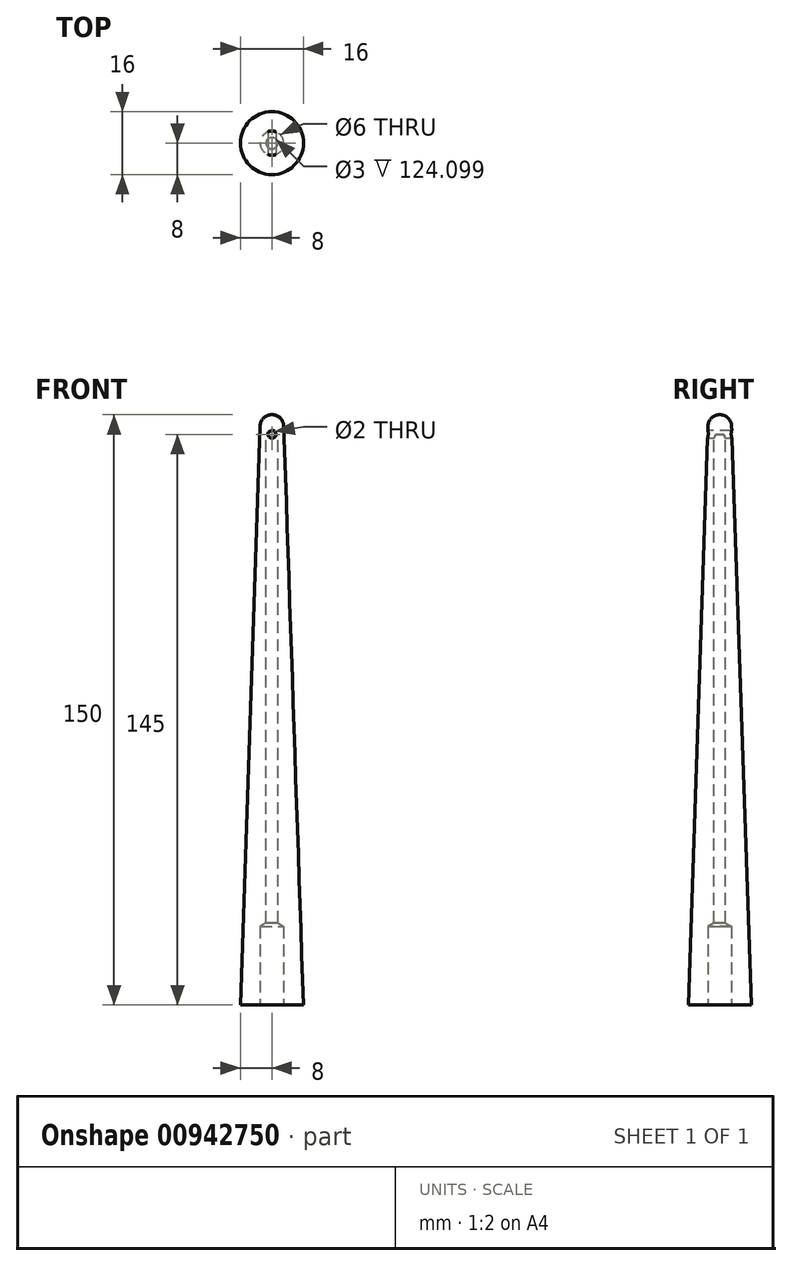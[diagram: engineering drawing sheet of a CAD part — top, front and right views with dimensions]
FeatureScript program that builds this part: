
annotation { "Feature Type Name" : "Feature", "Feature Type Description" : "" }
export const myFeature = defineFeature(function(context is Context, id is Id, definition is map)
    precondition{}
    {
        {
            var Q0;
            Q0=qCreatedBy(makeId("Front.planeOp"),FACE);
            var sketch = newSketch(context, id + "F0", { "sketchPlane" : qUnion([Q0])});
            skLineSegment(sketch, "E0", {"start": v(0, 0) * mm, "end": v(-8, 0) * mm});
            skLineSegment(sketch, "E1", {"start": v(-8, 0) * mm, "end": v(-3, 147.1) * mm});
            skLineSegment(sketch, "E2", {"start": v(0, 145) * mm, "end": v(0, 150) * mm});
            skLineSegment(sketch, "E3", {"start": v(0, 0) * mm, "end": v(0, -30.03) * mm, "construction": true});
            skArc(sketch, "E4", {"start": v(0, 150) * mm, "mid": v(-2.09, 149.16) * mm, "end": v(-3, 147.1) * mm});
            skLineSegment(sketch, "E5", {"start": v(-1.5, 0) * mm, "end": v(-1.5, 145) * mm});
            skLineSegment(sketch, "E6", {"start": v(-1.5, 145) * mm, "end": v(0, 145) * mm});
            skSolve(sketch);
        }
        {
            var Q0;
            Q0 = qSketchRegion(id + "F0", true);
            var Q1;
            Q1=sQuery(id+"F0.wireOp",EDGE,"E3");
            revolve(context, id + "F1", {"surfaceOperationType" : NewSurfaceOperationType.NEW, "entities" : qUnion([Q0]), "axis" : qUnion([Q1]), "revolveType" : RevolveType.FULL});
        }
        {
            var Q0;
            Q0=makeQuery(id+"F1.opRevolve","SWEPT_FACE",FACE,{"disambiguationData":[OSD([sQuery(id+"F0.wireOp",EDGE,"E0")])]});
            var sketch = newSketch(context, id + "F2", { "sketchPlane" : qUnion([Q0])});
            skPoint(sketch, "E7", {"position": v(0, 0) * mm});
            skSolve(sketch);
        }
        {
            var Q0;
            Q0=sQuery(id+"F2.wireOp",VERTEX,"E7");
            var Q1;
            Q1=makeQuery(id+"F1.opRevolve","SWEPT_BODY",BODY,{"disambiguationData":[OSD([sQuery(id+"F0.wireOp",EDGE,"E0"),sQuery(id+"F0.wireOp",EDGE,"E1"),sQuery(id+"F0.wireOp",EDGE,"E2"),sQuery(id+"F0.wireOp",EDGE,"E4")])]});
            hole(context, id + "F3", {"style" : HoleStyle.SIMPLE, "endStyle" : HoleEndStyle.BLIND, "holeDiameter" : 6 * mm, "majorDiameter" : 5 * mm, "holeDepth" : 20 * mm, "isTappedThrough" : true, "tappedDepth" : 12 * mm, "tapClearance" : 3, "locations" : qUnion([Q0]), "scope" : qUnion([Q1])});
        }
        {
            var Q0;
            Q0=qCreatedBy(makeId("Front.planeOp"),FACE);
            var sketch = newSketch(context, id + "F4", { "sketchPlane" : qUnion([Q0])});
            skCircle(sketch, "E8", {"center": v(0, 145) * mm, "radius": 1 * mm});
            skSolve(sketch);
        }
        {
            var Q0;
            Q0 = qSketchRegion(id + "F4", true);
            extrude(context, id + "F5", {"entities" : qUnion([Q0]), "operationType" : NewBodyOperationType.REMOVE, "endBound" : BoundingType.THROUGH_ALL, "oppositeDirection" : true, "depth" : 25 * mm, "offsetDistance" : 25 * mm, "hasSecondDirection" : true, "secondDirectionBound" : SecondDirectionBoundingType.THROUGH_ALL, "secondDirectionOppositeDirection" : false, "secondDirectionDepth" : 25 * mm});
        }
    });
